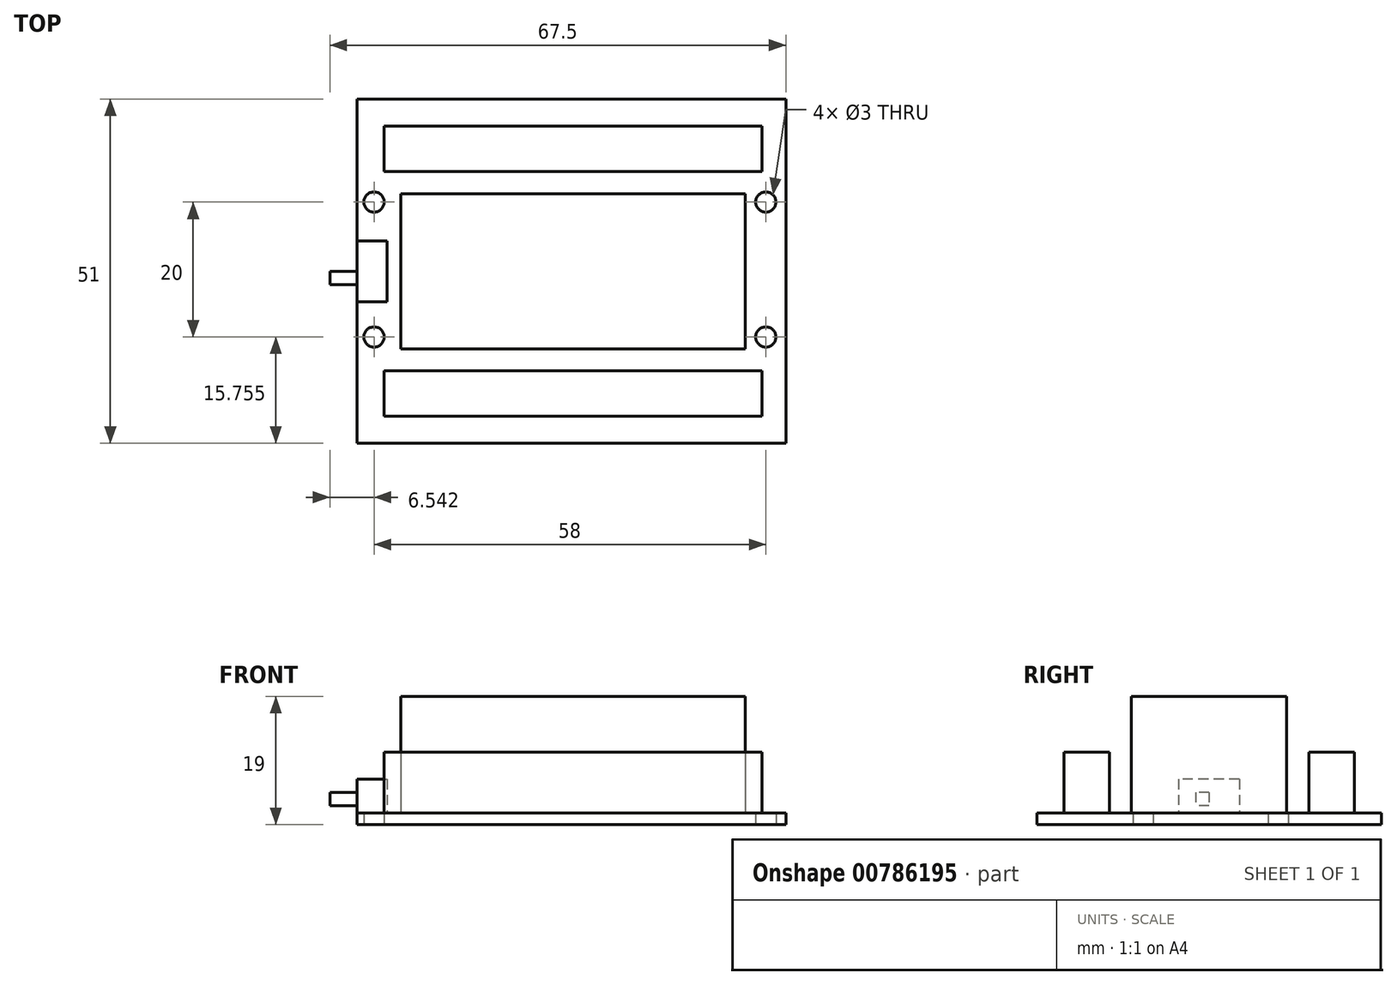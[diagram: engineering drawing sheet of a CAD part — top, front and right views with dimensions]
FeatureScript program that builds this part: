
annotation { "Feature Type Name" : "Feature", "Feature Type Description" : "" }
export const myFeature = defineFeature(function(context is Context, id is Id, definition is map)
    precondition{}
    {
        {
            assignVariable(context, id + "F0", {"name" : "board_thickness", "anyValue" : 1.7 * mm});
        }
        {
            assignVariable(context, id + "F1", {"name" : "terminalblock_height", "anyValue" : 9 * mm});
        }
        {
            assignVariable(context, id + "F2", {"name" : "switchbox_height", "anyValue" : 5 * mm});
        }
        {
            assignVariable(context, id + "F3", {"name" : "switch_length", "anyValue" : 4 * mm});
        }
        {
            var Q0;
            Q0=qCreatedBy(makeId("Top.planeOp"),FACE);
            var sketch = newSketch(context, id + "F4", { "sketchPlane" : qUnion([Q0])});
            skLineSegment(sketch, "E0.bottom", {"start": v(-9.58, 23.23) * mm, "end": v(53.92, 23.23) * mm});
            skLineSegment(sketch, "E0.top", {"start": v(-9.58, -27.77) * mm, "end": v(53.92, -27.77) * mm});
            skLineSegment(sketch, "E0.left", {"start": v(-9.58, 23.23) * mm, "end": v(-9.58, -27.77) * mm});
            skLineSegment(sketch, "E0.right", {"start": v(53.92, 23.23) * mm, "end": v(53.92, -27.77) * mm});
            skCircle(sketch, "E1", {"center": v(-7.04, 7.99) * mm, "radius": 1.5 * mm});
            skCircle(sketch, "E2.0.1.0", {"center": v(-7.04, -12.01) * mm, "radius": 1.5 * mm});
            skCircle(sketch, "E2.1.0.0", {"center": v(50.96, 7.99) * mm, "radius": 1.5 * mm});
            skCircle(sketch, "E2.1.1.0", {"center": v(50.96, -12.01) * mm, "radius": 1.5 * mm});
            skLineSegment(sketch, "E2.direction1", {"start": v(-7.04, 7.99) * mm, "end": v(50.96, 7.99) * mm, "construction": true});
            skLineSegment(sketch, "E2.direction2", {"start": v(-7.04, 7.99) * mm, "end": v(-7.04, -12.01) * mm, "construction": true});
            skSolve(sketch);
        }
        {
            var Q0;
            Q0=makeQuery(id+"F4.imprint","IMPRINT",FACE,{"disambiguationData":[TD([[makeQuery(id+"F4.imprint","IMPRINT",EDGE,{"derivedFrom":sQuery(id+"F4.wireOp",EDGE,"E0.bottom")}),-1.0]])]});
            extrude(context, id + "F5", {"entities" : qUnion([Q0]), "depth" : getVariable(context, 'board_thickness'), "offsetDistance" : 25 * mm});
        }
        {
            var Q0;
            Q0=makeQuery(id+"F5.opExtrude","CAP_FACE",FACE,{"disambiguationData":[OSD([sQuery(id+"F4.wireOp",EDGE,"E0.bottom"),sQuery(id+"F4.wireOp",EDGE,"E0.top"),sQuery(id+"F4.wireOp",EDGE,"E0.left"),sQuery(id+"F4.wireOp",EDGE,"E0.right"),sQuery(id+"F4.wireOp",EDGE,"E1"),sQuery(id+"F4.wireOp",EDGE,"E2.0.1.0"),sQuery(id+"F4.wireOp",EDGE,"E2.1.0.0"),sQuery(id+"F4.wireOp",EDGE,"E2.1.1.0")])],"isStart":false});
            var sketch = newSketch(context, id + "F6", { "sketchPlane" : qUnion([Q0])});
            skLineSegment(sketch, "E3", {"start": v(-9.58, -2.27) * mm, "end": v(53.92, -2.27) * mm, "construction": true});
            skLineSegment(sketch, "E4.bottom", {"start": v(-3.05, 9.23) * mm, "end": v(47.95, 9.23) * mm});
            skLineSegment(sketch, "E4.top", {"start": v(-3.05, -13.77) * mm, "end": v(47.95, -13.77) * mm});
            skLineSegment(sketch, "E4.left", {"start": v(-3.05, 9.23) * mm, "end": v(-3.05, -13.77) * mm});
            skLineSegment(sketch, "E4.right", {"start": v(47.95, 9.23) * mm, "end": v(47.95, -13.77) * mm});
            skLineSegment(sketch, "E5.bottom", {"start": v(-5.58, 12.48) * mm, "end": v(50.42, 12.48) * mm});
            skLineSegment(sketch, "E5.top", {"start": v(-5.58, 19.23) * mm, "end": v(50.42, 19.23) * mm});
            skLineSegment(sketch, "E5.left", {"start": v(50.42, 19.23) * mm, "end": v(50.42, 12.48) * mm});
            skLineSegment(sketch, "E5.right", {"start": v(-5.58, 19.23) * mm, "end": v(-5.58, 12.48) * mm});
            skLineSegment(sketch, "E6.bottom", {"start": v(-9.58, -6.77) * mm, "end": v(-5.13, -6.77) * mm});
            skLineSegment(sketch, "E6.top", {"start": v(-9.58, 2.23) * mm, "end": v(-5.13, 2.23) * mm});
            skLineSegment(sketch, "E6.left", {"start": v(-9.58, -6.77) * mm, "end": v(-9.58, 2.23) * mm});
            skLineSegment(sketch, "E6.right", {"start": v(-5.13, -6.77) * mm, "end": v(-5.13, 2.23) * mm});
            skLineSegment(sketch, "E7.MirrorCS", {"start": v(-5.58, -23.77) * mm, "end": v(50.42, -23.77) * mm});
            skLineSegment(sketch, "E8.MirrorCS", {"start": v(-5.58, -23.77) * mm, "end": v(-5.58, -17.02) * mm});
            skLineSegment(sketch, "E9.MirrorCS", {"start": v(-5.58, -17.02) * mm, "end": v(50.42, -17.02) * mm});
            skLineSegment(sketch, "E10.MirrorCS", {"start": v(50.42, -23.77) * mm, "end": v(50.42, -17.02) * mm});
            skPoint(sketch, "E11", {"position": v(-5.13, -2.27) * mm});
            skPoint(sketch, "E12", {"position": v(-3.05, -2.27) * mm});
            skSolve(sketch);
        }
        {
            var Q0;
            Q0=makeQuery(id+"F6.imprint","IMPRINT",FACE,{"disambiguationData":[TD([[makeQuery(id+"F6.imprint","IMPRINT",EDGE,{"derivedFrom":sQuery(id+"F6.wireOp",EDGE,"E4.bottom")}),-1.0]])]});
            extrude(context, id + "F7", {"entities" : qUnion([Q0]), "operationType" : NewBodyOperationType.ADD, "depth" : 17.3 * mm, "offsetDistance" : 25 * mm});
        }
        {
            var Q0;
            Q0=makeQuery(id+"F6.imprint","IMPRINT",FACE,{"disambiguationData":[TD([[makeQuery(id+"F6.imprint","IMPRINT",EDGE,{"derivedFrom":sQuery(id+"F6.wireOp",EDGE,"E5.bottom")}),1.0]])]});
            var Q1;
            Q1=makeQuery(id+"F6.imprint","IMPRINT",FACE,{"disambiguationData":[TD([[makeQuery(id+"F6.imprint","IMPRINT",EDGE,{"derivedFrom":sQuery(id+"F6.wireOp",EDGE,"E7.MirrorCS")}),1.0]])]});
            extrude(context, id + "F8", {"entities" : qUnion([Q0, Q1]), "operationType" : NewBodyOperationType.ADD, "depth" : getVariable(context, 'terminalblock_height'), "offsetDistance" : 25 * mm});
        }
        {
            var Q0;
            Q0=makeQuery(id+"F6.imprint","IMPRINT",FACE,{"disambiguationData":[TD([[makeQuery(id+"F6.imprint","IMPRINT",EDGE,{"derivedFrom":sQuery(id+"F6.wireOp",EDGE,"E6.bottom")}),1.0]])]});
            extrude(context, id + "F9", {"entities" : qUnion([Q0]), "operationType" : NewBodyOperationType.ADD, "depth" : getVariable(context, 'switchbox_height'), "offsetDistance" : 25 * mm});
        }
        {
            var Q0;
            Q0=makeQuery(id+"F9.boolean.opBoolean","MERGE",FACE,{"derivedFrom":[makeQuery(id+"F5.opExtrude","SWEPT_FACE",FACE,{"disambiguationData":[OSD([sQuery(id+"F4.wireOp",EDGE,"E0.left")])]}),makeQuery(id+"F9.opExtrude","SWEPT_FACE",FACE,{"disambiguationData":[OSD([sQuery(id+"F6.wireOp",EDGE,"E6.left")])]})]});
            var sketch = newSketch(context, id + "F10", { "sketchPlane" : qUnion([Q0])});
            skLineSegment(sketch, "E13.bottom", {"start": v(-2.23, 6.7) * mm, "end": v(6.77, 6.7) * mm});
            skLineSegment(sketch, "E13.top", {"start": v(-2.23, 6.7) * mm, "end": v(6.77, 6.7) * mm});
            skLineSegment(sketch, "E13.left", {"start": v(-2.23, 6.7) * mm, "end": v(-2.23, 6.7) * mm});
            skLineSegment(sketch, "E13.right", {"start": v(6.77, 6.7) * mm, "end": v(6.77, 6.7) * mm});
            skLineSegment(sketch, "E14.bottom", {"start": v(6.77, 1.7) * mm, "end": v(-2.23, 1.7) * mm});
            skLineSegment(sketch, "E14.top", {"start": v(6.77, 1.7) * mm, "end": v(-2.23, 1.7) * mm});
            skLineSegment(sketch, "E14.left", {"start": v(6.77, 1.7) * mm, "end": v(6.77, 1.7) * mm});
            skLineSegment(sketch, "E14.right", {"start": v(-2.23, 1.7) * mm, "end": v(-2.23, 1.7) * mm});
            skLineSegment(sketch, "E15.top", {"start": v(-2.23, 1.7) * mm, "end": v(6.77, 1.7) * mm});
            skLineSegment(sketch, "E15.left", {"start": v(-2.23, 6.7) * mm, "end": v(-2.23, 1.7) * mm});
            skLineSegment(sketch, "E15.right", {"start": v(6.77, 6.7) * mm, "end": v(6.77, 1.7) * mm});
            skLineSegment(sketch, "E16.bottom", {"start": v(2.27, 4.78) * mm, "end": v(4.27, 4.78) * mm});
            skLineSegment(sketch, "E16.top", {"start": v(2.27, 2.78) * mm, "end": v(4.27, 2.78) * mm});
            skLineSegment(sketch, "E16.left", {"start": v(2.27, 4.78) * mm, "end": v(2.27, 2.78) * mm});
            skLineSegment(sketch, "E16.right", {"start": v(4.27, 4.78) * mm, "end": v(4.27, 2.78) * mm});
            skSolve(sketch);
        }
        {
            var Q0;
            Q0=makeQuery(id+"F10.imprint","IMPRINT",FACE,{"disambiguationData":[TD([[makeQuery(id+"F10.imprint","IMPRINT",EDGE,{"derivedFrom":sQuery(id+"F10.wireOp",EDGE,"E16.bottom")}),-1.0]])]});
            extrude(context, id + "F11", {"entities" : qUnion([Q0]), "operationType" : NewBodyOperationType.ADD, "depth" : getVariable(context, 'switch_length'), "offsetDistance" : 25 * mm});
        }
    });
